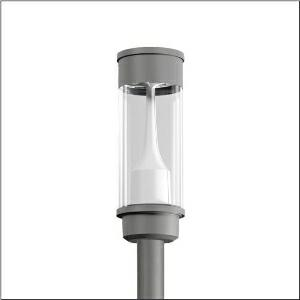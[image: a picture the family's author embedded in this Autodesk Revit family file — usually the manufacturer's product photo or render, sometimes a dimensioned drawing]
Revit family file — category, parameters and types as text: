
# Revit family: litepole_iq___st1_2a_5xa5415af14h_245c
name_source: partatom
category: Lighting Fixtures
units: mm (PartAtom-declared; Revit-internal decimal feet)

## family parameters
Cut with Voids When Loaded = No
Host = Face
Light Source = No
Part Type = Normal
Room Calculation Point = No
Round Connector Dimension = Use Diameter
Shared = No

## types (1)
- --- (1 x LED, 1540 lm, 12.9 W, 2200K)
    Apparent Load = 13 VA
    CIE Flux Codes = 22 61 93 96 100
    Color Rendering = 70
    Color Temperature = 2200K
    Default Elevation = 1800 mm
    Description = Litepole iQ, mast luminaire, Module 540 iQ-SR, primary light control with 3 zone facetted reflector, of plastic, silver coated, highly specular, structured, primary optical cover: cover, of PMMA, transparent, partly coated, light distribution: ST1.2a, light emission: direct distribution, primary light characteristic: asymmetric, installation type: post-top, LED, High Power LED, rated luminous flux: 1.540lm, luminous efficacy: 119lm/W, light colour: 722, colour temperature: 2200K, control gear: iQ Street-Remote, control: optimised constant luminous flux control (CLO 2.0), Desk-Remote (wireless, voltage-free reading and setting of iQ features in the workshop via application-optimized NFC function/RFID function), Light-Fading, Smart-Wire, Night-Set, Lumen-Switch, Temp-Guard, Auto-Match, Street-Remote, pre-setting: logarithmic dimming characteristic, with terminal, 6-pole, max. 2.5mm², mains connection: 230..240V, AC, 50/60Hz, start of lifetime: 13W, end of service life: 13W, reduction: 6W, luminaire housing, upper part, of glass-fibre reinforced polyester, coated, Siteco® metallic grey (DB 702S), diameter: 210mm, height: 590mm, spigot size: d x l = 76 x 70mm (post-top) | with reducer (optional accessory) 60 x 70mm, mounting height: 3..5m, post-top mast mounting element, of diecast aluminium, coated, Siteco® metallic grey (DB 702S), Module 540 iQ-SR, traffic white (RAL 9016), equipment: standard, protection rating (complete): IP65, insulation class (complete): insulation class II (safety insulation), certification: CE, ENEC, VDE, packaging unit: 1 piece

Light Distribution: ST1.2a
    Height = 590 mm
    Lamp = 1 x LED
    Lamp Light Flux = 1540 lm
    Lamp Power = 12.9 W
    Lamp count = 1
    Length = 220 mm
    Luminous efficacy = 119 lm/W
    Manufacturer = Siteco
    ModVariant = No
    Model = 5XA5415AF14H
    Number of Poles = 1
    OnlyDefault = Yes
    Power Factor = 1
    Product Name = Litepole iQ | ST1.2a
    Product group = mast luminaire | pylon top
    ProductGroupID = 6100
    Protection Class = Protection class II
    Protection Degree = IP 65
    RLX_Detail_Level = 1
    RLX_Emergency_Light_Flux = 0 lm
    RLX_Emergency_Type = 0
    RLX_Emergency_Type_DB = No
    RlxData = <blob elided: 72737 chars, md5=0b314d91>
    Socket = socket
    Standby Power = 0 W
    System Light Flux = 1540 lm
    System Power = 13 W
    Type Comments = factory setting: luminous flux: 100 % | dim-lin: 254 | 516 mA
    Type Image = l_1006025.jpg
    URL = http://relux.com
    VarID = @adj_180357
    Voltage = 0 V
    Weight = 0.00 kg
    Width = 0 mm  [stored 0 ft]

note: [stored X ft] marks values corroborated as IEEE doubles in the binary element streams (Revit-internal decimal feet)

## geometry (parser evidence)
native form markers: Blend x4, Sweep x11
no freeform markers — native parametric forms only
